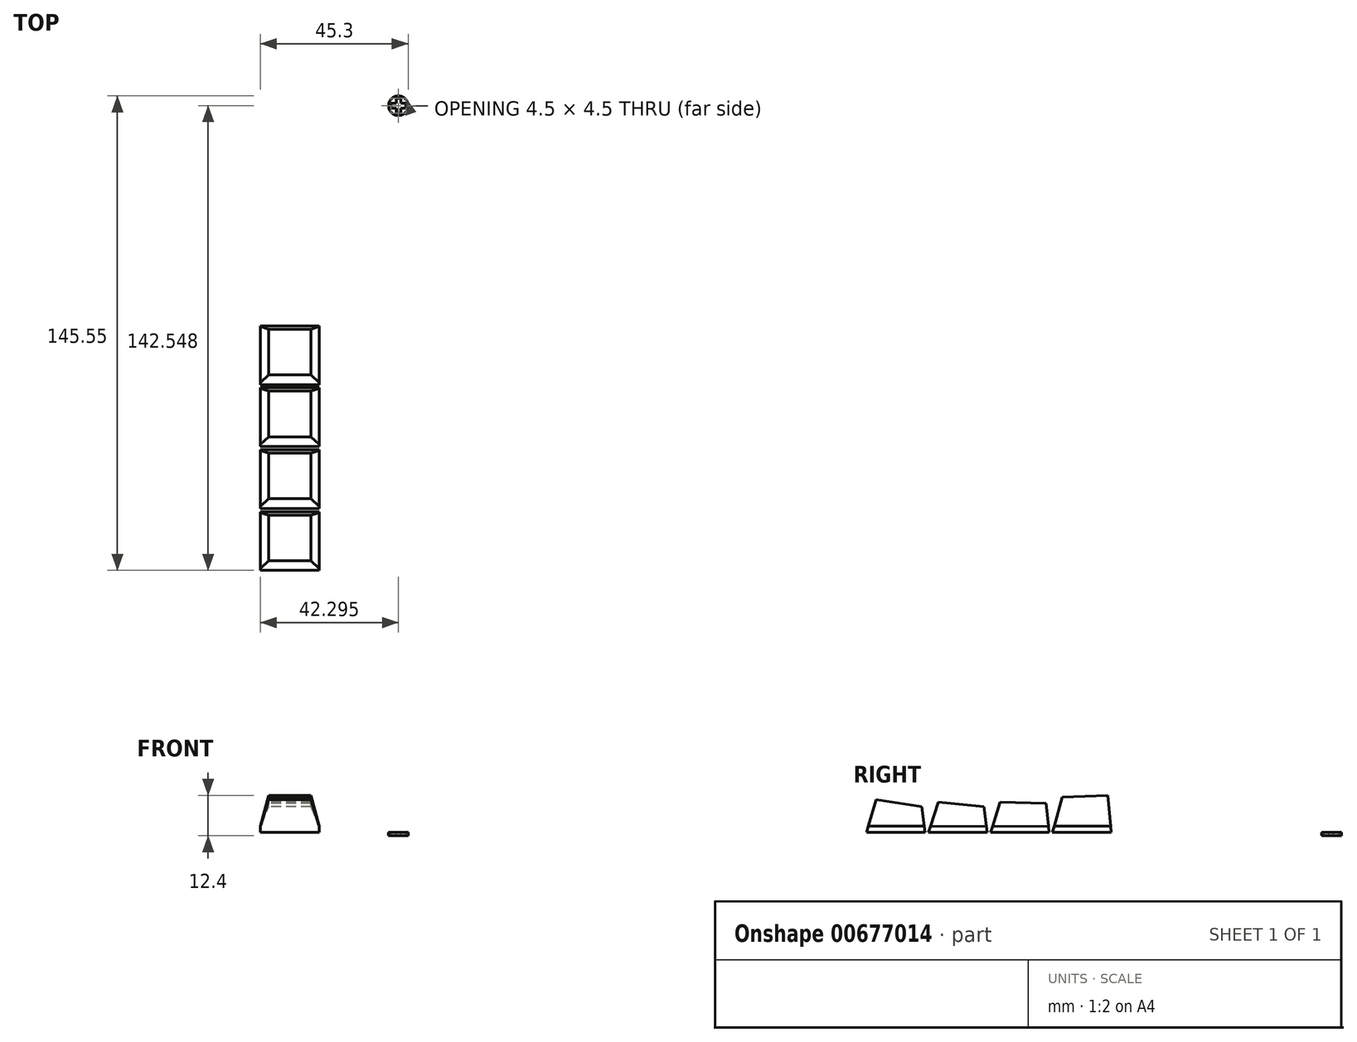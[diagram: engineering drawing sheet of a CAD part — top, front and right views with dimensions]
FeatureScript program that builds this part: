
annotation { "Feature Type Name" : "Feature", "Feature Type Description" : "" }
export const myFeature = defineFeature(function(context is Context, id is Id, definition is map)
    precondition{}
    {
        {
            var Q0;
            Q0=qCreatedBy(makeId("Right.planeOp"),FACE);
            var sketch = newSketch(context, id + "F0", { "sketchPlane" : qUnion([Q0])});
            skLineSegment(sketch, "E0", {"start": v(0, 0) * mm, "end": v(-1, 11.4) * mm});
            skLineSegment(sketch, "E1", {"start": v(-1, 11.4) * mm, "end": v(-15, 10.8) * mm});
            skLineSegment(sketch, "E2", {"start": v(-15, 10.8) * mm, "end": v(-18, 0) * mm});
            skLineSegment(sketch, "E3", {"start": v(-18, 0) * mm, "end": v(0, 0) * mm});
            skLineSegment(sketch, "E4", {"start": v(-19, 0) * mm, "end": v(-20, 9) * mm});
            skLineSegment(sketch, "E5", {"start": v(-20, 9) * mm, "end": v(-34, 9.3) * mm});
            skLineSegment(sketch, "E6", {"start": v(-34, 9.3) * mm, "end": v(-37, 0) * mm});
            skLineSegment(sketch, "E7", {"start": v(-37, 0) * mm, "end": v(-19, 0) * mm});
            skLineSegment(sketch, "E8", {"start": v(-38, 0) * mm, "end": v(-39, 8) * mm});
            skLineSegment(sketch, "E9", {"start": v(-39, 8) * mm, "end": v(-53, 9.3) * mm});
            skLineSegment(sketch, "E10", {"start": v(-53, 9.3) * mm, "end": v(-56, 0) * mm});
            skLineSegment(sketch, "E11", {"start": v(-56, 0) * mm, "end": v(-38, 0) * mm});
            skLineSegment(sketch, "E12", {"start": v(-57, 0) * mm, "end": v(-58, 7.9) * mm});
            skLineSegment(sketch, "E13", {"start": v(-58, 7.9) * mm, "end": v(-72, 10.1) * mm});
            skLineSegment(sketch, "E14", {"start": v(-72, 10.1) * mm, "end": v(-75, 0) * mm});
            skLineSegment(sketch, "E15", {"start": v(-75, 0) * mm, "end": v(-57, 0) * mm});
            skSolve(sketch);
        }
        {
            var Q0;
            Q0 = qSketchRegion(id + "F0", true);
            extrude(context, id + "F1", {"entities" : qUnion([Q0]), "depth" : 18 * mm, "offsetDistance" : 25 * mm});
        }
        {
            var Q0;
            Q0=makeQuery(id+"F1.opExtrude","SWEPT_FACE",FACE,{"disambiguationData":[OSD([sQuery(id+"F0.wireOp",EDGE,"E8")])]});
            var sketch = newSketch(context, id + "F2", { "sketchPlane" : qUnion([Q0])});
            skLineSegment(sketch, "E16", {"start": v(-18, 6.71) * mm, "end": v(-18, 12.78) * mm});
            skLineSegment(sketch, "E17", {"start": v(-18, 12.78) * mm, "end": v(-15.5, 12.78) * mm});
            skLineSegment(sketch, "E18", {"start": v(-15.5, 12.78) * mm, "end": v(-18, 6.71) * mm});
            skLineSegment(sketch, "E19", {"start": v(0, 6.71) * mm, "end": v(-2.5, 12.78) * mm});
            skLineSegment(sketch, "E20", {"start": v(-2.5, 12.78) * mm, "end": v(0, 12.78) * mm});
            skLineSegment(sketch, "E21", {"start": v(0, 12.78) * mm, "end": v(0, 6.71) * mm});
            skSolve(sketch);
        }
        {
            var Q0;
            Q0=makeQuery(id+"F1.opExtrude","SWEPT_FACE",FACE,{"disambiguationData":[OSD([sQuery(id+"F0.wireOp",EDGE,"E10")])]});
            var sketch = newSketch(context, id + "F3", { "sketchPlane" : qUnion([Q0])});
            skLineSegment(sketch, "E22", {"start": v(18, -15.2) * mm, "end": v(15.5, -7.42) * mm});
            skLineSegment(sketch, "E23", {"start": v(15.5, -7.42) * mm, "end": v(18, -7.42) * mm});
            skLineSegment(sketch, "E24", {"start": v(18, -7.42) * mm, "end": v(18, -15.2) * mm});
            skLineSegment(sketch, "E25", {"start": v(0, -15.2) * mm, "end": v(0, -7.42) * mm});
            skLineSegment(sketch, "E26", {"start": v(0, -7.42) * mm, "end": v(2.5, -7.42) * mm});
            skLineSegment(sketch, "E27", {"start": v(2.5, -7.42) * mm, "end": v(0, -15.2) * mm});
            skSolve(sketch);
        }
        {
            var Q1;
            Q1=makeQuery(id+"F2.imprint","IMPRINT",FACE,{"disambiguationData":[TD([[makeQuery(id+"F2.imprint","IMPRINT",EDGE,{"derivedFrom":sQuery(id+"F2.wireOp",EDGE,"E16")}),-1.0]])]});
            var Q2;
            Q2=makeQuery(id+"F3.imprint","IMPRINT",FACE,{"disambiguationData":[TD([[makeQuery(id+"F3.imprint","IMPRINT",EDGE,{"derivedFrom":sQuery(id+"F3.wireOp",EDGE,"E22")}),-1.0]])]});
            loft(context, id + "F4", {"operationType" : NewBodyOperationType.REMOVE, "sheetProfilesArray" : [{ "sheetProfileEntities" : qUnion([Q1]) }, { "sheetProfileEntities" : qUnion([Q2]) }]});
        }
        {
            var Q1;
            Q1=makeQuery(id+"F2.imprint","IMPRINT",FACE,{"disambiguationData":[TD([[makeQuery(id+"F2.imprint","IMPRINT",EDGE,{"derivedFrom":sQuery(id+"F2.wireOp",EDGE,"E19")}),-1.0]])]});
            var Q2;
            Q2=makeQuery(id+"F3.imprint","IMPRINT",FACE,{"disambiguationData":[TD([[makeQuery(id+"F3.imprint","IMPRINT",EDGE,{"derivedFrom":sQuery(id+"F3.wireOp",EDGE,"E25")}),1.0]])]});
            loft(context, id + "F5", {"operationType" : NewBodyOperationType.REMOVE, "sheetProfilesArray" : [{ "sheetProfileEntities" : qUnion([Q1]) }, { "sheetProfileEntities" : qUnion([Q2]) }]});
        }
        {
            var Q0;
            Q0=makeQuery(id+"F1.opExtrude","SWEPT_FACE",FACE,{"disambiguationData":[OSD([sQuery(id+"F0.wireOp",EDGE,"E12")])]});
            var sketch = newSketch(context, id + "F6", { "sketchPlane" : qUnion([Q0])});
            skLineSegment(sketch, "E28", {"start": v(-18, 9.16) * mm, "end": v(-18, 15.12) * mm});
            skLineSegment(sketch, "E29", {"start": v(-18, 15.12) * mm, "end": v(-15.5, 15.12) * mm});
            skLineSegment(sketch, "E30", {"start": v(-15.5, 15.12) * mm, "end": v(-18, 9.16) * mm});
            skLineSegment(sketch, "E31", {"start": v(0, 9.16) * mm, "end": v(-2.5, 15.12) * mm});
            skLineSegment(sketch, "E32", {"start": v(-2.5, 15.12) * mm, "end": v(0, 15.12) * mm});
            skLineSegment(sketch, "E33", {"start": v(0, 15.12) * mm, "end": v(0, 9.16) * mm});
            skSolve(sketch);
        }
        {
            var Q0;
            Q0=makeQuery(id+"F1.opExtrude","SWEPT_FACE",FACE,{"disambiguationData":[OSD([sQuery(id+"F0.wireOp",EDGE,"E14")])]});
            var sketch = newSketch(context, id + "F7", { "sketchPlane" : qUnion([Q0])});
            skLineSegment(sketch, "E34", {"start": v(0, -19.36) * mm, "end": v(0, -10.82) * mm});
            skLineSegment(sketch, "E35", {"start": v(0, -10.82) * mm, "end": v(2.5, -10.82) * mm});
            skLineSegment(sketch, "E36", {"start": v(2.5, -10.82) * mm, "end": v(0, -19.36) * mm});
            skLineSegment(sketch, "E37", {"start": v(15.5, -10.82) * mm, "end": v(18, -19.36) * mm});
            skLineSegment(sketch, "E38", {"start": v(18, -19.36) * mm, "end": v(18, -10.82) * mm});
            skLineSegment(sketch, "E39", {"start": v(18, -10.82) * mm, "end": v(15.5, -10.82) * mm});
            skSolve(sketch);
        }
        {
            var Q1;
            Q1=makeQuery(id+"F6.imprint","IMPRINT",FACE,{"disambiguationData":[TD([[makeQuery(id+"F6.imprint","IMPRINT",EDGE,{"derivedFrom":sQuery(id+"F6.wireOp",EDGE,"E28")}),-1.0]])]});
            var Q2;
            Q2=makeQuery(id+"F7.imprint","IMPRINT",FACE,{"disambiguationData":[TD([[makeQuery(id+"F7.imprint","IMPRINT",EDGE,{"derivedFrom":sQuery(id+"F7.wireOp",EDGE,"E37")}),1.0]])]});
            loft(context, id + "F8", {"operationType" : NewBodyOperationType.REMOVE, "sheetProfilesArray" : [{ "sheetProfileEntities" : qUnion([Q1]) }, { "sheetProfileEntities" : qUnion([Q2]) }]});
        }
        {
            var Q1;
            Q1=makeQuery(id+"F6.imprint","IMPRINT",FACE,{"disambiguationData":[TD([[makeQuery(id+"F6.imprint","IMPRINT",EDGE,{"derivedFrom":sQuery(id+"F6.wireOp",EDGE,"E31")}),-1.0]])]});
            var Q2;
            Q2=makeQuery(id+"F7.imprint","IMPRINT",FACE,{"disambiguationData":[TD([[makeQuery(id+"F7.imprint","IMPRINT",EDGE,{"derivedFrom":sQuery(id+"F7.wireOp",EDGE,"E34")}),1.0]])]});
            loft(context, id + "F9", {"operationType" : NewBodyOperationType.REMOVE, "sheetProfilesArray" : [{ "sheetProfileEntities" : qUnion([Q1]) }, { "sheetProfileEntities" : qUnion([Q2]) }]});
        }
        {
            var Q0;
            Q0=makeQuery(id+"F1.opExtrude","SWEPT_FACE",FACE,{"disambiguationData":[OSD([sQuery(id+"F0.wireOp",EDGE,"E4")])]});
            var sketch = newSketch(context, id + "F10", { "sketchPlane" : qUnion([Q0])});
            skLineSegment(sketch, "E40", {"start": v(-18, 4.1) * mm, "end": v(-18, 11.15) * mm});
            skLineSegment(sketch, "E41", {"start": v(-18, 11.15) * mm, "end": v(-15.5, 11.15) * mm});
            skLineSegment(sketch, "E42", {"start": v(-15.5, 11.15) * mm, "end": v(-18, 4.1) * mm});
            skLineSegment(sketch, "E43", {"start": v(-2.5, 11.15) * mm, "end": v(0, 4.1) * mm});
            skLineSegment(sketch, "E44", {"start": v(0, 4.1) * mm, "end": v(0, 11.15) * mm});
            skLineSegment(sketch, "E45", {"start": v(0, 11.15) * mm, "end": v(-2.5, 11.15) * mm});
            skSolve(sketch);
        }
        {
            var Q0;
            Q0=makeQuery(id+"F1.opExtrude","SWEPT_FACE",FACE,{"disambiguationData":[OSD([sQuery(id+"F0.wireOp",EDGE,"E6")])]});
            var sketch = newSketch(context, id + "F11", { "sketchPlane" : qUnion([Q0])});
            skLineSegment(sketch, "E46", {"start": v(18, -9.36) * mm, "end": v(15.5, -1.59) * mm});
            skLineSegment(sketch, "E47", {"start": v(15.5, -1.59) * mm, "end": v(18, -1.59) * mm});
            skLineSegment(sketch, "E48", {"start": v(18, -1.59) * mm, "end": v(18, -9.36) * mm});
            skLineSegment(sketch, "E49", {"start": v(2.5, -1.59) * mm, "end": v(0, -1.59) * mm});
            skLineSegment(sketch, "E50", {"start": v(0, -1.59) * mm, "end": v(0, -9.36) * mm});
            skLineSegment(sketch, "E51", {"start": v(0, -9.36) * mm, "end": v(2.5, -1.59) * mm});
            skSolve(sketch);
        }
        {
            var Q1;
            Q1=makeQuery(id+"F11.imprint","IMPRINT",FACE,{"disambiguationData":[TD([[makeQuery(id+"F11.imprint","IMPRINT",EDGE,{"derivedFrom":sQuery(id+"F11.wireOp",EDGE,"E46")}),-1.0]])]});
            var Q2;
            Q2=makeQuery(id+"F10.imprint","IMPRINT",FACE,{"disambiguationData":[TD([[makeQuery(id+"F10.imprint","IMPRINT",EDGE,{"derivedFrom":sQuery(id+"F10.wireOp",EDGE,"E40")}),-1.0]])]});
            loft(context, id + "F12", {"operationType" : NewBodyOperationType.REMOVE, "sheetProfilesArray" : [{ "sheetProfileEntities" : qUnion([Q1]) }, { "sheetProfileEntities" : qUnion([Q2]) }]});
        }
        {
            var Q1;
            Q1=makeQuery(id+"F10.imprint","IMPRINT",FACE,{"disambiguationData":[TD([[makeQuery(id+"F10.imprint","IMPRINT",EDGE,{"derivedFrom":sQuery(id+"F10.wireOp",EDGE,"E43")}),1.0]])]});
            var Q2;
            Q2=makeQuery(id+"F11.imprint","IMPRINT",FACE,{"disambiguationData":[TD([[makeQuery(id+"F11.imprint","IMPRINT",EDGE,{"derivedFrom":sQuery(id+"F11.wireOp",EDGE,"E49")}),1.0]])]});
            loft(context, id + "F13", {"operationType" : NewBodyOperationType.REMOVE, "sheetProfilesArray" : [{ "sheetProfileEntities" : qUnion([Q1]) }, { "sheetProfileEntities" : qUnion([Q2]) }]});
        }
        {
            var Q0;
            Q0=makeQuery(id+"F1.opExtrude","SWEPT_FACE",FACE,{"disambiguationData":[OSD([sQuery(id+"F0.wireOp",EDGE,"E0")])]});
            var sketch = newSketch(context, id + "F14", { "sketchPlane" : qUnion([Q0])});
            skLineSegment(sketch, "E52", {"start": v(-18, 2) * mm, "end": v(-18, 11.44) * mm});
            skLineSegment(sketch, "E53", {"start": v(-18, 11.44) * mm, "end": v(-15.5, 11.44) * mm});
            skLineSegment(sketch, "E54", {"start": v(-15.5, 11.44) * mm, "end": v(-18, 2) * mm});
            skLineSegment(sketch, "E55", {"start": v(0, 2) * mm, "end": v(-2.5, 11.44) * mm});
            skLineSegment(sketch, "E56", {"start": v(-2.5, 11.44) * mm, "end": v(0, 11.44) * mm});
            skLineSegment(sketch, "E57", {"start": v(0, 11.44) * mm, "end": v(0, 2) * mm});
            skSolve(sketch);
        }
        {
            var Q0;
            Q0=makeQuery(id+"F1.opExtrude","SWEPT_FACE",FACE,{"disambiguationData":[OSD([sQuery(id+"F0.wireOp",EDGE,"E2")])]});
            var sketch = newSketch(context, id + "F15", { "sketchPlane" : qUnion([Q0])});
            skLineSegment(sketch, "E58", {"start": v(18, -2.82) * mm, "end": v(15.5, 6.4) * mm});
            skLineSegment(sketch, "E59", {"start": v(15.5, 6.4) * mm, "end": v(18, 6.4) * mm});
            skLineSegment(sketch, "E60", {"start": v(18, 6.4) * mm, "end": v(18, -2.82) * mm});
            skLineSegment(sketch, "E61", {"start": v(2.5, 6.4) * mm, "end": v(0, 6.4) * mm});
            skLineSegment(sketch, "E62", {"start": v(0, 6.4) * mm, "end": v(0, -2.82) * mm});
            skLineSegment(sketch, "E63", {"start": v(0, -2.82) * mm, "end": v(2.5, 6.4) * mm});
            skSolve(sketch);
        }
        {
            var Q1;
            Q1=makeQuery(id+"F15.imprint","IMPRINT",FACE,{"disambiguationData":[TD([[makeQuery(id+"F15.imprint","IMPRINT",EDGE,{"derivedFrom":sQuery(id+"F15.wireOp",EDGE,"E61")}),1.0]])]});
            var Q2;
            Q2=makeQuery(id+"F14.imprint","IMPRINT",FACE,{"disambiguationData":[TD([[makeQuery(id+"F14.imprint","IMPRINT",EDGE,{"derivedFrom":sQuery(id+"F14.wireOp",EDGE,"E55")}),-1.0]])]});
            loft(context, id + "F16", {"operationType" : NewBodyOperationType.REMOVE, "sheetProfilesArray" : [{ "sheetProfileEntities" : qUnion([Q1]) }, { "sheetProfileEntities" : qUnion([Q2]) }]});
        }
        {
            var Q1;
            Q1=makeQuery(id+"F14.imprint","IMPRINT",FACE,{"disambiguationData":[TD([[makeQuery(id+"F14.imprint","IMPRINT",EDGE,{"derivedFrom":sQuery(id+"F14.wireOp",EDGE,"E52")}),-1.0]])]});
            var Q2;
            Q2=makeQuery(id+"F15.imprint","IMPRINT",FACE,{"disambiguationData":[TD([[makeQuery(id+"F15.imprint","IMPRINT",EDGE,{"derivedFrom":sQuery(id+"F15.wireOp",EDGE,"E58")}),-1.0]])]});
            loft(context, id + "F17", {"operationType" : NewBodyOperationType.REMOVE, "sheetProfilesArray" : [{ "sheetProfileEntities" : qUnion([Q1]) }, { "sheetProfileEntities" : qUnion([Q2]) }]});
        }
        {
            var Q0;
            Q0=qCreatedBy(makeId("Top.planeOp"),FACE);
            var sketch = newSketch(context, id + "F18", { "sketchPlane" : qUnion([Q0])});
            skCircle(sketch, "E64", {"center": v(42.3, 67.55) * mm, "radius": 3 * mm});
            skLineSegment(sketch, "E65", {"start": v(34.8, 67.55) * mm, "end": v(49.67, 67.55) * mm, "construction": true});
            skLineSegment(sketch, "E66", {"start": v(42.3, 72.29) * mm, "end": v(42.3, 62) * mm, "construction": true});
            skLineSegment(sketch, "E67", {"start": v(41.6, 68.25) * mm, "end": v(41.6, 69.8) * mm});
            skLineSegment(sketch, "E68", {"start": v(41.6, 69.8) * mm, "end": v(43, 69.8) * mm});
            skLineSegment(sketch, "E69", {"start": v(43, 69.8) * mm, "end": v(43, 68.25) * mm});
            skLineSegment(sketch, "E70", {"start": v(43, 68.25) * mm, "end": v(44.55, 68.25) * mm});
            skLineSegment(sketch, "E71", {"start": v(44.55, 68.25) * mm, "end": v(44.55, 66.85) * mm});
            skLineSegment(sketch, "E72", {"start": v(44.55, 66.85) * mm, "end": v(43, 66.85) * mm});
            skLineSegment(sketch, "E73", {"start": v(43, 66.85) * mm, "end": v(43, 65.3) * mm});
            skLineSegment(sketch, "E74", {"start": v(43, 65.3) * mm, "end": v(41.6, 65.3) * mm});
            skLineSegment(sketch, "E75", {"start": v(41.6, 65.3) * mm, "end": v(41.6, 66.85) * mm});
            skLineSegment(sketch, "E76", {"start": v(41.6, 66.85) * mm, "end": v(40.05, 66.85) * mm});
            skLineSegment(sketch, "E77", {"start": v(40.05, 66.85) * mm, "end": v(40.05, 68.25) * mm});
            skLineSegment(sketch, "E78", {"start": v(40.05, 68.25) * mm, "end": v(41.6, 68.25) * mm});
            skSolve(sketch);
        }
        {
            var Q0;
            Q0 = qSketchRegion(id + "F18", true);
            extrude(context, id + "F19", {"entities" : qUnion([Q0]), "oppositeDirection" : true, "depth" : 1 * mm, "offsetDistance" : 25 * mm});
        }
    });
